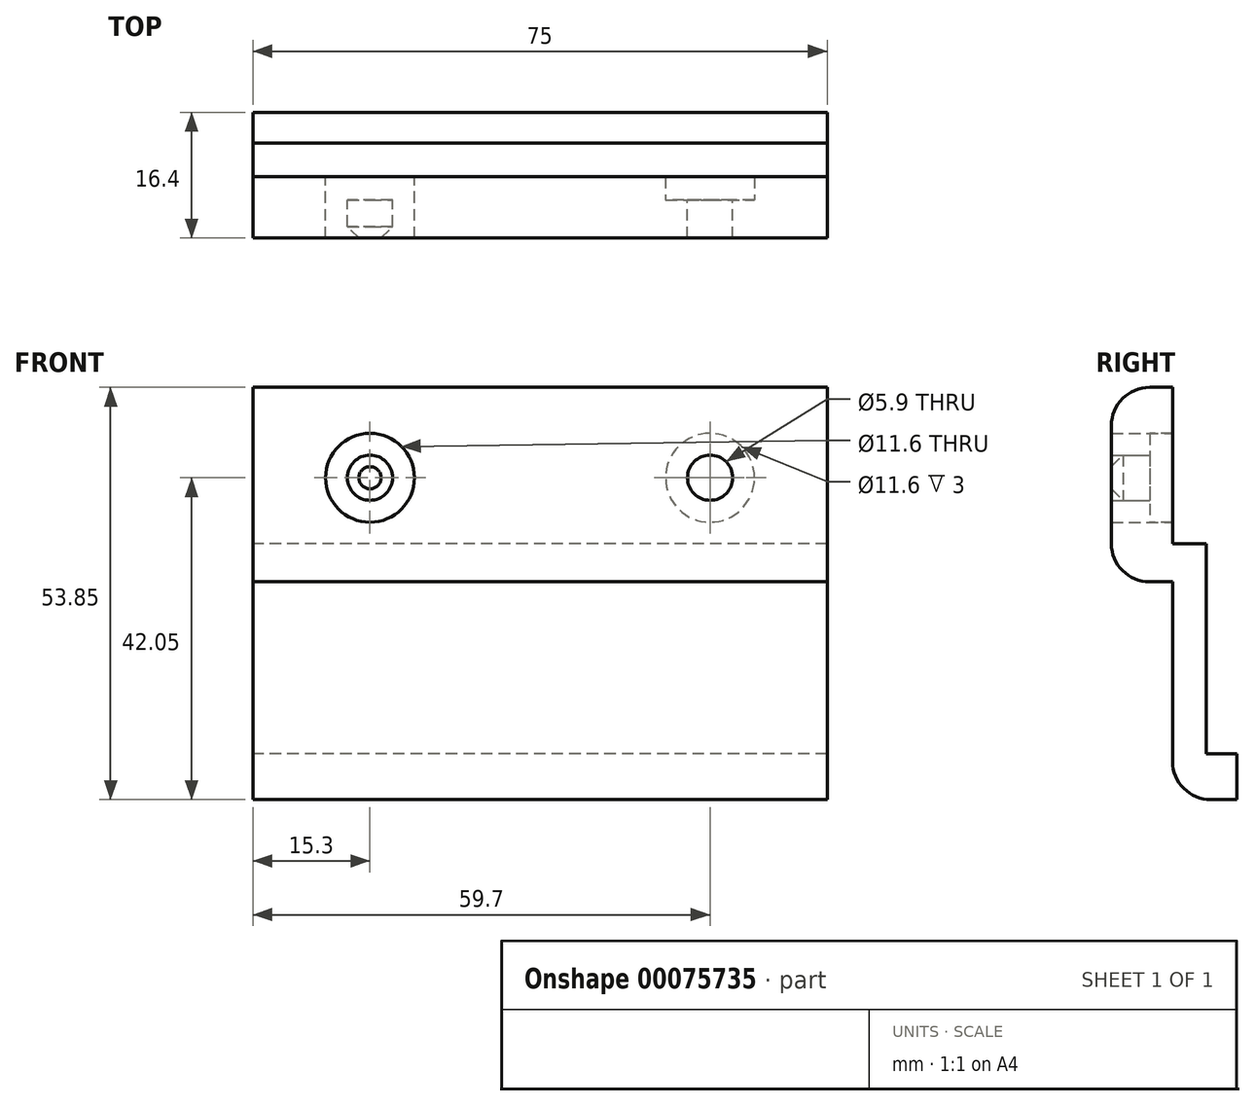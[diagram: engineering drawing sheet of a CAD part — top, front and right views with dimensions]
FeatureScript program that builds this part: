
annotation { "Feature Type Name" : "Feature", "Feature Type Description" : "" }
export const myFeature = defineFeature(function(context is Context, id is Id, definition is map)
    precondition{}
    {
        {
            var Q0;
            Q0=qCreatedBy(makeId("Right.planeOp"),FACE);
            var sketch = newSketch(context, id + "F0", { "sketchPlane" : qUnion([Q0])});
            skLineSegment(sketch, "E0", {"start": v(0, 20.4) * mm, "end": v(-8, 20.4) * mm});
            skLineSegment(sketch, "E1", {"start": v(0, 20.4) * mm, "end": v(0, 14.4) * mm});
            skLineSegment(sketch, "E2", {"start": v(0, 0) * mm, "end": v(4.4, 0) * mm});
            skLineSegment(sketch, "E3", {"start": v(4.4, 0) * mm, "end": v(4.4, -27.45) * mm});
            skLineSegment(sketch, "E4", {"start": v(4.4, -27.45) * mm, "end": v(8.4, -27.45) * mm});
            skLineSegment(sketch, "E5", {"start": v(8.4, -27.45) * mm, "end": v(8.4, -33.45) * mm});
            skLineSegment(sketch, "E6", {"start": v(8.4, -33.45) * mm, "end": v(0, -33.45) * mm});
            skLineSegment(sketch, "E7", {"start": v(0, -33.45) * mm, "end": v(0, -5) * mm});
            skLineSegment(sketch, "E8", {"start": v(0, -5) * mm, "end": v(-8, -5) * mm});
            skLineSegment(sketch, "E9.bottom", {"start": v(0, 14.4) * mm, "end": v(-3, 14.4) * mm});
            skLineSegment(sketch, "E9.top", {"start": v(0, 2.8) * mm, "end": v(-3, 2.8) * mm});
            skLineSegment(sketch, "E9.right", {"start": v(-3, 14.4) * mm, "end": v(-3, 2.8) * mm});
            skLineSegment(sketch, "E10.trimOffspring", {"start": v(0, 2.8) * mm, "end": v(0, 0) * mm});
            skLineSegment(sketch, "E11", {"start": v(-8, 20.4) * mm, "end": v(-8, -5) * mm});
            skSolve(sketch);
        }
        {
            var Q0;
            Q0=makeQuery(id+"F0.imprint","IMPRINT",FACE,{"disambiguationData":[TD([[makeQuery(id+"F0.imprint","IMPRINT",EDGE,{"derivedFrom":sQuery(id+"F0.wireOp",EDGE,"E0")}),1.0]])]});
            extrude(context, id + "F1", {"entities" : qUnion([Q0]), "depth" : 75 * mm});
        }
        {
            var Q0;
            Q0=makeQuery(id+"F1.opExtrude","SWEPT_FACE",FACE,{"disambiguationData":[OSD([sQuery(id+"F0.wireOp",EDGE,"E9.right")])]});
            var sketch = newSketch(context, id + "F2", { "sketchPlane" : qUnion([Q0])});
            skLineSegment(sketch, "E12.0.0", {"start": v(0, 2.8) * mm, "end": v(0, 14.4) * mm});
            skLineSegment(sketch, "E12.0.1", {"start": v(0, 14.4) * mm, "end": v(-75, 14.4) * mm});
            skLineSegment(sketch, "E12.0.2", {"start": v(-75, 14.4) * mm, "end": v(-75, 2.8) * mm});
            skLineSegment(sketch, "E12.0.3", {"start": v(-75, 2.8) * mm, "end": v(0, 2.8) * mm});
            skLineSegment(sketch, "E13", {"start": v(-37.5, 14.4) * mm, "end": v(-37.5, 2.8) * mm, "construction": true});
            skCircle(sketch, "E14", {"center": v(-59.7, 8.6) * mm, "radius": 5.8 * mm});
            skPoint(sketch, "E14.centerSnap0", {"position": v(-37.5, 8.6) * mm});
            skCircle(sketch, "E15", {"center": v(-59.7, 8.6) * mm, "radius": 2.95 * mm});
            skCircle(sketch, "E16.MirrorC", {"center": v(-15.3, 8.6) * mm, "radius": 2.95 * mm});
            skCircle(sketch, "E17.MirrorC", {"center": v(-15.3, 8.6) * mm, "radius": 5.8 * mm});
            skSolve(sketch);
        }
        {
            var Q0;
            Q0=makeQuery(id+"F2.imprint","IMPRINT",FACE,{"disambiguationData":[TD([[makeQuery(id+"F2.imprint","IMPRINT",EDGE,{"derivedFrom":sQuery(id+"F2.wireOp",EDGE,"E15")}),1.0]])]});
            var Q1;
            Q1=makeQuery(id+"F2.imprint","IMPRINT",FACE,{"disambiguationData":[TD([[makeQuery(id+"F2.imprint","IMPRINT",EDGE,{"derivedFrom":sQuery(id+"F2.wireOp",EDGE,"E16.MirrorC")}),-1.0]])]});
            var Q2;
            Q2=sQuery(id+"F2.wireOp",EDGE,"E15");
            var Q3;
            Q3=sQuery(id+"F2.wireOp",EDGE,"E16.MirrorC");
            var Q4;
            Q4=makeQuery(id+"F1.opExtrude","SWEPT_FACE",FACE,{"disambiguationData":[OSD([sQuery(id+"F0.wireOp",EDGE,"E11")])]});
            extrude(context, id + "F3", {"entities" : qUnion([Q0, Q1]), "operationType" : NewBodyOperationType.REMOVE, "surfaceEntities" : qUnion([Q2, Q3]), "endBound" : BoundingType.UP_TO_SURFACE, "oppositeDirection" : true, "endBoundEntityFace" : qUnion([Q4]), "depth" : 25 * mm});
        }
        {
            var Q0;
            {var subQ0=sQuery(id+"F2.wireOp",EDGE,"E12.0.2");Q0=makeQuery(id+"F2.imprint","IMPRINT",FACE,{"disambiguationData":[TD([[makeQuery(id+"F2.imprint","IMPRINT",EDGE,{"derivedFrom":subQ0}),1.0]])]});}
            var Q1;
            {var subQ0=sQuery(id+"F2.wireOp",EDGE,"E12.0.0");Q1=makeQuery(id+"F2.imprint","IMPRINT",FACE,{"disambiguationData":[TD([[makeQuery(id+"F2.imprint","IMPRINT",EDGE,{"derivedFrom":subQ0}),-1.0]])]});}
            var Q2;
            {var subQ0=sQuery(id+"F2.wireOp",EDGE,"E14");var subQ1=sQuery(id+"F2.wireOp",EDGE,"E12.0.1");var subQ2=makeQuery(id+"F2.imprint","INTERSECT",VERTEX,{"derivedFrom":[subQ1,subQ0]});Q2=makeQuery(id+"F2.imprint","IMPRINT",FACE,{"disambiguationData":[TD([[makeQuery(id+"F2.imprint","IMPRINT",EDGE,{"disambiguationData":[TD([[subQ2,-1.0]])],"derivedFrom":subQ1}),-1.0]])]});}
            var Q3;
            Q3=makeQuery(id+"F1.opExtrude","SWEPT_FACE",FACE,{"disambiguationData":[OSD([sQuery(id+"F0.wireOp",EDGE,"E1")])]});
            extrude(context, id + "F4", {"entities" : qUnion([Q0, Q1, Q2]), "operationType" : NewBodyOperationType.ADD, "endBound" : BoundingType.UP_TO_SURFACE, "endBoundEntityFace" : qUnion([Q3]), "depth" : 25 * mm});
        }
        {
            var Q0;
            Q0=makeQuery(id+"F1.opExtrude","SWEPT_EDGE",EDGE,{"disambiguationData":[OSD([sQuery(id+"F0.wireOp",EDGE,"E0"),sQuery(id+"F0.wireOp",EDGE,"E11")])]});
            var Q1;
            Q1=makeQuery(id+"F1.opExtrude","SWEPT_EDGE",EDGE,{"disambiguationData":[OSD([sQuery(id+"F0.wireOp",EDGE,"E8"),sQuery(id+"F0.wireOp",EDGE,"E11")])]});
            var Q2;
            Q2=makeQuery(id+"F1.opExtrude","SWEPT_EDGE",EDGE,{"disambiguationData":[OSD([sQuery(id+"F0.wireOp",EDGE,"E6"),sQuery(id+"F0.wireOp",EDGE,"E7")])]});
            fillet(context, id + "F5", {"entities" : qUnion([Q0, Q1, Q2]), "radius" : 5 * mm, "tangentPropagation" : true, "allowEdgeOverflow" : false});
        }
        {
            var Q0;
            Q0=makeQuery(id+"F3.boolean.opBoolean","COPY",EDGE,{"derivedFrom":makeQuery(id+"F3.opExtrude","CAP_EDGE",EDGE,{"disambiguationData":[OSD([sQuery(id+"F2.wireOp",EDGE,"E16.MirrorC")])],"isStart":false})});
            var Q1;
            Q1=makeQuery(id+"F3.boolean.opBoolean","COPY",EDGE,{"derivedFrom":makeQuery(id+"F3.opExtrude","CAP_EDGE",EDGE,{"disambiguationData":[OSD([sQuery(id+"F2.wireOp",EDGE,"E15")])],"isStart":false})});
            chamfer(context, id + "F6", {"entities" : qUnion([Q0, Q1]), "width" : 1.5 * mm, "tangentPropagation" : true});
        }
    });
